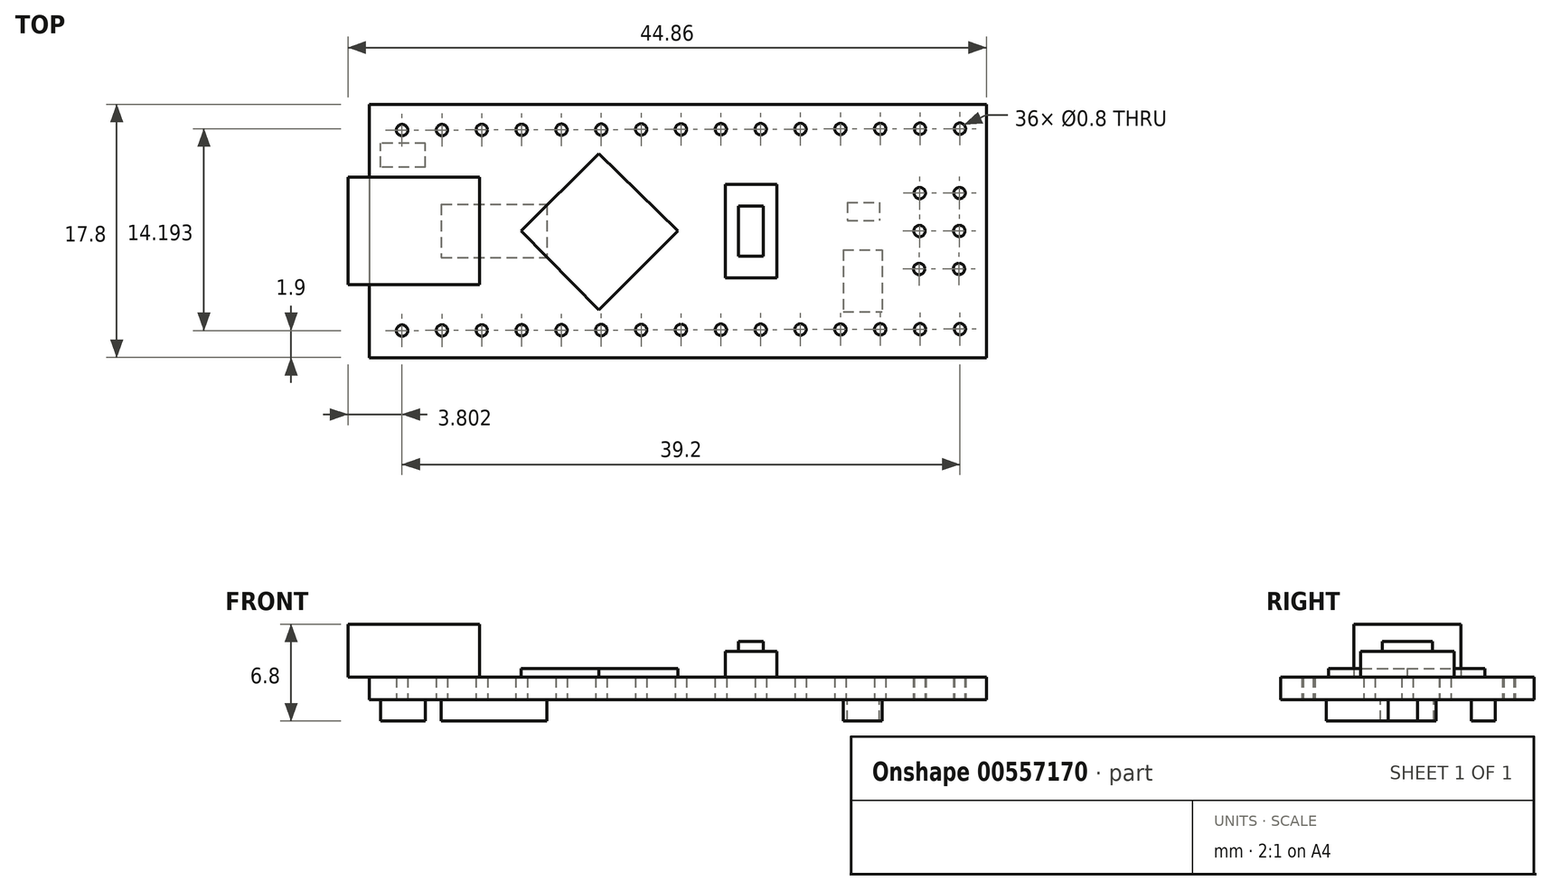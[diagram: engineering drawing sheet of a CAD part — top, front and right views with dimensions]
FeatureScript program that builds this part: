
annotation { "Feature Type Name" : "Feature", "Feature Type Description" : "" }
export const myFeature = defineFeature(function(context is Context, id is Id, definition is map)
    precondition{}
    {
        {
            var Q0;
            Q0=qCreatedBy(makeId("Top.planeOp"),FACE);
            var sketch = newSketch(context, id + "F0", { "sketchPlane" : qUnion([Q0])});
            skLineSegment(sketch, "E0.bottom", {"start": v(21.68, 8.9) * mm, "end": v(-21.67, 8.9) * mm});
            skLineSegment(sketch, "E0.top", {"start": v(21.67, -8.9) * mm, "end": v(-21.68, -8.9) * mm});
            skLineSegment(sketch, "E0.left", {"start": v(21.68, 8.9) * mm, "end": v(21.67, -8.9) * mm});
            skLineSegment(sketch, "E0.right", {"start": v(-21.67, 8.9) * mm, "end": v(-21.68, -8.9) * mm});
            skPoint(sketch, "E0.middle", {"position": v(0, 0) * mm});
            skCircle(sketch, "E1", {"center": v(-19.38, 7.1) * mm, "radius": 0.4 * mm});
            skCircle(sketch, "E2.0.3.0", {"center": v(94.43, 7.36) * mm, "radius": 0.4 * mm});
            skCircle(sketch, "E2.0.4.0", {"center": v(132.33, 7.36) * mm, "radius": 0.4 * mm});
            skCircle(sketch, "E3.1.0.0", {"center": v(-16.58, 7.1) * mm, "radius": 0.4 * mm});
            skCircle(sketch, "E3.2.0.0", {"center": v(-13.78, 7.1) * mm, "radius": 0.4 * mm});
            skCircle(sketch, "E3.3.0.0", {"center": v(-10.98, 7.11) * mm, "radius": 0.4 * mm});
            skCircle(sketch, "E3.4.0.0", {"center": v(-8.18, 7.12) * mm, "radius": 0.4 * mm});
            skCircle(sketch, "E3.5.0.0", {"center": v(-5.38, 7.13) * mm, "radius": 0.4 * mm});
            skCircle(sketch, "E3.6.0.0", {"center": v(-2.58, 7.14) * mm, "radius": 0.4 * mm});
            skCircle(sketch, "E3.7.0.0", {"center": v(0.22, 7.14) * mm, "radius": 0.4 * mm});
            skCircle(sketch, "E3.8.0.0", {"center": v(3.02, 7.15) * mm, "radius": 0.4 * mm});
            skCircle(sketch, "E3.9.0.0", {"center": v(5.82, 7.16) * mm, "radius": 0.4 * mm});
            skCircle(sketch, "E3.10.0.0", {"center": v(8.62, 7.16) * mm, "radius": 0.4 * mm});
            skCircle(sketch, "E3.11.0.0", {"center": v(11.42, 7.17) * mm, "radius": 0.4 * mm});
            skCircle(sketch, "E3.12.0.0", {"center": v(14.22, 7.18) * mm, "radius": 0.4 * mm});
            skCircle(sketch, "E3.13.0.0", {"center": v(17.02, 7.19) * mm, "radius": 0.4 * mm});
            skCircle(sketch, "E3.14.0.0", {"center": v(19.82, 7.2) * mm, "radius": 0.4 * mm});
            skLineSegment(sketch, "E4", {"start": v(-5.56, -6.44) * mm, "end": v(-0.12, -1) * mm});
            skLineSegment(sketch, "E5", {"start": v(-5.56, -6.44) * mm, "end": v(-11, -1) * mm});
            skLineSegment(sketch, "E6", {"start": v(-0.12, -1) * mm, "end": v(-5.56, 4.45) * mm});
            skLineSegment(sketch, "E7", {"start": v(-11, -1) * mm, "end": v(-5.56, 4.45) * mm});
            skLineSegment(sketch, "E8.bottom", {"start": v(3.33, -3.28) * mm, "end": v(6.96, -3.28) * mm});
            skLineSegment(sketch, "E8.top", {"start": v(3.33, 3.28) * mm, "end": v(6.96, 3.28) * mm});
            skLineSegment(sketch, "E8.left", {"start": v(3.33, -3.28) * mm, "end": v(3.33, 3.28) * mm});
            skLineSegment(sketch, "E8.right", {"start": v(6.96, -3.28) * mm, "end": v(6.96, 3.28) * mm});
            skPoint(sketch, "E8.middle", {"position": v(5.14, 0) * mm});
            skLineSegment(sketch, "E9.bottom", {"start": v(4.27, -1.76) * mm, "end": v(6.01, -1.76) * mm});
            skLineSegment(sketch, "E9.top", {"start": v(4.27, 1.76) * mm, "end": v(6.01, 1.76) * mm});
            skLineSegment(sketch, "E9.left", {"start": v(4.27, -1.76) * mm, "end": v(4.27, 1.76) * mm});
            skLineSegment(sketch, "E9.right", {"start": v(6.01, -1.76) * mm, "end": v(6.01, 1.76) * mm});
            skCircle(sketch, "E10.1.0.0", {"center": v(19.8, 2.67) * mm, "radius": 0.4 * mm});
            skCircle(sketch, "E10.1.0.1", {"center": v(17, 2.66) * mm, "radius": 0.4 * mm});
            skCircle(sketch, "E10.2.0.0", {"center": v(19.78, 0) * mm, "radius": 0.4 * mm});
            skCircle(sketch, "E10.2.0.1", {"center": v(16.98, 0) * mm, "radius": 0.4 * mm});
            skCircle(sketch, "E10.3.0.0", {"center": v(19.76, -2.66) * mm, "radius": 0.4 * mm});
            skCircle(sketch, "E10.3.0.1", {"center": v(16.96, -2.67) * mm, "radius": 0.4 * mm});
            skCircle(sketch, "E11", {"center": v(-19.38, -7) * mm, "radius": 0.4 * mm});
            skCircle(sketch, "E12.1.0.0", {"center": v(-16.58, -7) * mm, "radius": 0.4 * mm});
            skCircle(sketch, "E12.2.0.0", {"center": v(-13.78, -6.99) * mm, "radius": 0.4 * mm});
            skCircle(sketch, "E12.3.0.0", {"center": v(-10.98, -6.98) * mm, "radius": 0.4 * mm});
            skCircle(sketch, "E12.4.0.0", {"center": v(-8.18, -6.97) * mm, "radius": 0.4 * mm});
            skCircle(sketch, "E12.5.0.0", {"center": v(-5.38, -6.96) * mm, "radius": 0.4 * mm});
            skCircle(sketch, "E12.6.0.0", {"center": v(-2.58, -6.96) * mm, "radius": 0.4 * mm});
            skCircle(sketch, "E12.7.0.0", {"center": v(0.22, -6.95) * mm, "radius": 0.4 * mm});
            skCircle(sketch, "E12.8.0.0", {"center": v(3.02, -6.94) * mm, "radius": 0.4 * mm});
            skCircle(sketch, "E12.9.0.0", {"center": v(5.82, -6.94) * mm, "radius": 0.4 * mm});
            skCircle(sketch, "E12.10.0.0", {"center": v(8.62, -6.93) * mm, "radius": 0.4 * mm});
            skCircle(sketch, "E12.11.0.0", {"center": v(11.42, -6.92) * mm, "radius": 0.4 * mm});
            skCircle(sketch, "E12.12.0.0", {"center": v(14.22, -6.91) * mm, "radius": 0.4 * mm});
            skCircle(sketch, "E12.13.0.0", {"center": v(17.02, -6.9) * mm, "radius": 0.4 * mm});
            skCircle(sketch, "E12.14.0.0", {"center": v(19.82, -6.9) * mm, "radius": 0.4 * mm});
            skLineSegment(sketch, "E13.bottom", {"start": v(-23.18, 3.77) * mm, "end": v(-13.94, 3.77) * mm});
            skLineSegment(sketch, "E13.top", {"start": v(-23.18, -3.77) * mm, "end": v(-13.94, -3.77) * mm});
            skLineSegment(sketch, "E13.left", {"start": v(-23.18, 3.77) * mm, "end": v(-23.18, -3.77) * mm});
            skLineSegment(sketch, "E13.right", {"start": v(-13.94, 3.77) * mm, "end": v(-13.94, -3.77) * mm});
            skPoint(sketch, "E13.middle", {"position": v(-18.56, 0) * mm});
            skPoint(sketch, "E13.middle.positionSnap0", {"position": v(-21.68, 0) * mm});
            skPoint(sketch, "E13.centerSnap0", {"position": v(-21.68, 0) * mm});
            skLineSegment(sketch, "E14", {"start": v(-21.68, 0) * mm, "end": v(21.68, 0) * mm, "construction": true});
            skSolve(sketch);
        }
        {
            var Q0;
            Q0=makeQuery(id+"F0.imprint","IMPRINT",FACE,{"disambiguationData":[TD([[makeQuery(id+"F0.imprint","IMPRINT",EDGE,{"derivedFrom":sQuery(id+"F0.wireOp",EDGE,"E0.bottom")}),1.0]])]});
            var Q1;
            {var subQ5=sQuery(id+"F0.wireOp",EDGE,"E13.right");Q1=makeQuery(id+"F0.imprint","IMPRINT",FACE,{"disambiguationData":[TD([[makeQuery(id+"F0.imprint","IMPRINT",EDGE,{"derivedFrom":subQ5}),-1.0]])]});}
            var Q2;
            Q2=makeQuery(id+"F0.imprint","IMPRINT",FACE,{"disambiguationData":[TD([[makeQuery(id+"F0.imprint","IMPRINT",EDGE,{"derivedFrom":sQuery(id+"F0.wireOp",EDGE,"E4")}),1.0]])]});
            var Q3;
            Q3=makeQuery(id+"F0.imprint","IMPRINT",FACE,{"disambiguationData":[TD([[makeQuery(id+"F0.imprint","IMPRINT",EDGE,{"derivedFrom":sQuery(id+"F0.wireOp",EDGE,"E8.bottom")}),1.0]])]});
            var Q4;
            Q4=makeQuery(id+"F0.imprint","IMPRINT",FACE,{"disambiguationData":[TD([[makeQuery(id+"F0.imprint","IMPRINT",EDGE,{"derivedFrom":sQuery(id+"F0.wireOp",EDGE,"E9.bottom")}),1.0]])]});
            extrude(context, id + "F1", {"entities" : qUnion([Q0, Q1, Q2, Q3, Q4]), "endBound" : BoundingType.SYMMETRIC, "depth" : 1.6 * mm, "offsetDistance" : 25 * mm});
        }
        {
            var Q0;
            Q0=makeQuery(id+"F1.opExtrude","CAP_FACE",FACE,{"disambiguationData":[OSD([sQuery(id+"F0.wireOp",EDGE,"E0.bottom"),sQuery(id+"F0.wireOp",EDGE,"E0.top"),sQuery(id+"F0.wireOp",EDGE,"E0.left"),sQuery(id+"F0.wireOp",EDGE,"E0.right"),sQuery(id+"F0.wireOp",EDGE,"E1"),sQuery(id+"F0.wireOp",EDGE,"E3.1.0.0"),sQuery(id+"F0.wireOp",EDGE,"E3.2.0.0"),sQuery(id+"F0.wireOp",EDGE,"E3.3.0.0"),sQuery(id+"F0.wireOp",EDGE,"E3.4.0.0"),sQuery(id+"F0.wireOp",EDGE,"E3.5.0.0"),sQuery(id+"F0.wireOp",EDGE,"E3.6.0.0"),sQuery(id+"F0.wireOp",EDGE,"E3.7.0.0"),sQuery(id+"F0.wireOp",EDGE,"E3.8.0.0"),sQuery(id+"F0.wireOp",EDGE,"E3.9.0.0"),sQuery(id+"F0.wireOp",EDGE,"E3.10.0.0"),sQuery(id+"F0.wireOp",EDGE,"E3.11.0.0"),sQuery(id+"F0.wireOp",EDGE,"E3.12.0.0"),sQuery(id+"F0.wireOp",EDGE,"E3.13.0.0"),sQuery(id+"F0.wireOp",EDGE,"E3.14.0.0"),sQuery(id+"F0.wireOp",EDGE,"E10.1.0.0"),sQuery(id+"F0.wireOp",EDGE,"E10.1.0.1"),sQuery(id+"F0.wireOp",EDGE,"E10.2.0.0"),sQuery(id+"F0.wireOp",EDGE,"E10.2.0.1"),sQuery(id+"F0.wireOp",EDGE,"E10.3.0.0"),sQuery(id+"F0.wireOp",EDGE,"E10.3.0.1"),sQuery(id+"F0.wireOp",EDGE,"E11"),sQuery(id+"F0.wireOp",EDGE,"E12.1.0.0"),sQuery(id+"F0.wireOp",EDGE,"E12.2.0.0"),sQuery(id+"F0.wireOp",EDGE,"E12.3.0.0"),sQuery(id+"F0.wireOp",EDGE,"E12.4.0.0"),sQuery(id+"F0.wireOp",EDGE,"E12.5.0.0"),sQuery(id+"F0.wireOp",EDGE,"E12.6.0.0"),sQuery(id+"F0.wireOp",EDGE,"E12.7.0.0"),sQuery(id+"F0.wireOp",EDGE,"E12.8.0.0"),sQuery(id+"F0.wireOp",EDGE,"E12.9.0.0"),sQuery(id+"F0.wireOp",EDGE,"E12.10.0.0"),sQuery(id+"F0.wireOp",EDGE,"E12.11.0.0"),sQuery(id+"F0.wireOp",EDGE,"E12.12.0.0"),sQuery(id+"F0.wireOp",EDGE,"E12.13.0.0"),sQuery(id+"F0.wireOp",EDGE,"E12.14.0.0")])],"isStart":false});
            var sketch = newSketch(context, id + "F2", { "sketchPlane" : qUnion([Q0])});
            skLineSegment(sketch, "E15.0", {"start": v(-23.18, 3.77) * mm, "end": v(-13.94, 3.77) * mm});
            skLineSegment(sketch, "E15.1", {"start": v(-13.94, 3.77) * mm, "end": v(-13.94, -3.77) * mm});
            skLineSegment(sketch, "E15.2", {"start": v(-23.18, -3.77) * mm, "end": v(-13.94, -3.77) * mm});
            skLineSegment(sketch, "E15.3", {"start": v(-23.18, 3.77) * mm, "end": v(-23.18, -3.77) * mm});
            skLineSegment(sketch, "E15.4", {"start": v(-11, 0) * mm, "end": v(-5.56, 5.44) * mm});
            skLineSegment(sketch, "E15.5", {"start": v(0, 0) * mm, "end": v(-5.56, 5.44) * mm});
            skLineSegment(sketch, "E15.6", {"start": v(-5.56, -5.54) * mm, "end": v(0, 0) * mm});
            skLineSegment(sketch, "E15.7", {"start": v(-5.56, -5.54) * mm, "end": v(-11, 0) * mm});
            skLineSegment(sketch, "E15.8", {"start": v(6.96, -3.28) * mm, "end": v(6.96, 3.28) * mm});
            skLineSegment(sketch, "E15.9", {"start": v(3.33, 3.28) * mm, "end": v(6.96, 3.28) * mm});
            skLineSegment(sketch, "E15.10", {"start": v(3.33, -3.28) * mm, "end": v(6.96, -3.28) * mm});
            skLineSegment(sketch, "E15.11", {"start": v(3.33, -3.28) * mm, "end": v(3.33, 3.28) * mm});
            skLineSegment(sketch, "E15.12", {"start": v(4.27, 1.76) * mm, "end": v(6.01, 1.76) * mm});
            skLineSegment(sketch, "E15.13", {"start": v(6.01, -1.76) * mm, "end": v(6.01, 1.76) * mm});
            skLineSegment(sketch, "E15.14", {"start": v(4.27, -1.76) * mm, "end": v(4.27, 1.76) * mm});
            skLineSegment(sketch, "E15.15", {"start": v(4.27, -1.76) * mm, "end": v(6.01, -1.76) * mm});
            skLineSegment(sketch, "E16.0", {"start": v(-21.68, 0) * mm, "end": v(21.68, 0) * mm, "construction": true});
            skSolve(sketch);
        }
        {
            var Q0;
            {var subQ0=sQuery(id+"F2.wireOp",EDGE,"E15.3");Q0=makeQuery(id+"F2.imprint","IMPRINT",FACE,{"disambiguationData":[TD([[makeQuery(id+"F2.imprint","IMPRINT",EDGE,{"derivedFrom":subQ0}),1.0]])]});}
            var Q1;
            {var subQ0=sQuery(id+"F2.wireOp",EDGE,"E15.1");Q1=makeQuery(id+"F2.imprint","IMPRINT",FACE,{"disambiguationData":[TD([[makeQuery(id+"F2.imprint","IMPRINT",EDGE,{"derivedFrom":subQ0}),-1.0]])]});}
            extrude(context, id + "F3", {"entities" : qUnion([Q0, Q1]), "operationType" : NewBodyOperationType.ADD, "depth" : 3.7 * mm, "offsetDistance" : 25 * mm});
        }
        {
            var Q0;
            Q0=makeQuery(id+"F2.imprint","IMPRINT",FACE,{"disambiguationData":[TD([[makeQuery(id+"F2.imprint","IMPRINT",EDGE,{"derivedFrom":sQuery(id+"F2.wireOp",EDGE,"E15.4")}),-1.0]])]});
            var Q1;
            Q1=sQuery(id+"F0.wireOp",EDGE,"E7");
            var Q2;
            Q2=sQuery(id+"F0.wireOp",EDGE,"E6");
            var Q3;
            Q3=sQuery(id+"F0.wireOp",EDGE,"E4");
            var Q4;
            Q4=sQuery(id+"F0.wireOp",EDGE,"E5");
            extrude(context, id + "F4", {"entities" : qUnion([Q0]), "operationType" : NewBodyOperationType.ADD, "surfaceEntities" : qUnion([Q1, Q2, Q3, Q4]), "depth" : .6 * mm, "offsetDistance" : 25 * mm});
        }
        {
            var Q0;
            Q0=makeQuery(id+"F2.imprint","IMPRINT",FACE,{"disambiguationData":[TD([[makeQuery(id+"F2.imprint","IMPRINT",EDGE,{"derivedFrom":sQuery(id+"F2.wireOp",EDGE,"E15.8")}),1.0]])]});
            extrude(context, id + "F5", {"entities" : qUnion([Q0]), "operationType" : NewBodyOperationType.ADD, "depth" : 1.8 * mm, "offsetDistance" : 25 * mm});
        }
        {
            var Q0;
            Q0=makeQuery(id+"F2.imprint","IMPRINT",FACE,{"disambiguationData":[TD([[makeQuery(id+"F2.imprint","IMPRINT",EDGE,{"derivedFrom":sQuery(id+"F2.wireOp",EDGE,"E15.12")}),-1.0]])]});
            extrude(context, id + "F6", {"entities" : qUnion([Q0]), "operationType" : NewBodyOperationType.ADD, "depth" : 2.5 * mm, "offsetDistance" : 25 * mm});
        }
        {
            var Q0;
            Q0=makeQuery(id+"F1.opExtrude","CAP_FACE",FACE,{"disambiguationData":[OSD([sQuery(id+"F0.wireOp",EDGE,"E0.bottom"),sQuery(id+"F0.wireOp",EDGE,"E0.top"),sQuery(id+"F0.wireOp",EDGE,"E0.left"),sQuery(id+"F0.wireOp",EDGE,"E0.right"),sQuery(id+"F0.wireOp",EDGE,"E1"),sQuery(id+"F0.wireOp",EDGE,"E3.1.0.0"),sQuery(id+"F0.wireOp",EDGE,"E3.2.0.0"),sQuery(id+"F0.wireOp",EDGE,"E3.3.0.0"),sQuery(id+"F0.wireOp",EDGE,"E3.4.0.0"),sQuery(id+"F0.wireOp",EDGE,"E3.5.0.0"),sQuery(id+"F0.wireOp",EDGE,"E3.6.0.0"),sQuery(id+"F0.wireOp",EDGE,"E3.7.0.0"),sQuery(id+"F0.wireOp",EDGE,"E3.8.0.0"),sQuery(id+"F0.wireOp",EDGE,"E3.9.0.0"),sQuery(id+"F0.wireOp",EDGE,"E3.10.0.0"),sQuery(id+"F0.wireOp",EDGE,"E3.11.0.0"),sQuery(id+"F0.wireOp",EDGE,"E3.12.0.0"),sQuery(id+"F0.wireOp",EDGE,"E3.13.0.0"),sQuery(id+"F0.wireOp",EDGE,"E3.14.0.0"),sQuery(id+"F0.wireOp",EDGE,"E10.1.0.0"),sQuery(id+"F0.wireOp",EDGE,"E10.1.0.1"),sQuery(id+"F0.wireOp",EDGE,"E10.2.0.0"),sQuery(id+"F0.wireOp",EDGE,"E10.2.0.1"),sQuery(id+"F0.wireOp",EDGE,"E10.3.0.0"),sQuery(id+"F0.wireOp",EDGE,"E10.3.0.1"),sQuery(id+"F0.wireOp",EDGE,"E11"),sQuery(id+"F0.wireOp",EDGE,"E12.1.0.0"),sQuery(id+"F0.wireOp",EDGE,"E12.2.0.0"),sQuery(id+"F0.wireOp",EDGE,"E12.3.0.0"),sQuery(id+"F0.wireOp",EDGE,"E12.4.0.0"),sQuery(id+"F0.wireOp",EDGE,"E12.5.0.0"),sQuery(id+"F0.wireOp",EDGE,"E12.6.0.0"),sQuery(id+"F0.wireOp",EDGE,"E12.7.0.0"),sQuery(id+"F0.wireOp",EDGE,"E12.8.0.0"),sQuery(id+"F0.wireOp",EDGE,"E12.9.0.0"),sQuery(id+"F0.wireOp",EDGE,"E12.10.0.0"),sQuery(id+"F0.wireOp",EDGE,"E12.11.0.0"),sQuery(id+"F0.wireOp",EDGE,"E12.12.0.0"),sQuery(id+"F0.wireOp",EDGE,"E12.13.0.0"),sQuery(id+"F0.wireOp",EDGE,"E12.14.0.0")])],"isStart":true});
            var sketch = newSketch(context, id + "F7", { "sketchPlane" : qUnion([Q0])});
            skLineSegment(sketch, "E17.0", {"start": v(-21.68, 0) * mm, "end": v(21.68, 0) * mm, "construction": true});
            skLineSegment(sketch, "E18.bottom", {"start": v(-16.63, -1.87) * mm, "end": v(-9.2, -1.87) * mm});
            skLineSegment(sketch, "E18.top", {"start": v(-16.63, 1.87) * mm, "end": v(-9.2, 1.87) * mm});
            skLineSegment(sketch, "E18.left", {"start": v(-16.63, -1.87) * mm, "end": v(-16.63, 1.87) * mm});
            skLineSegment(sketch, "E18.right", {"start": v(-9.2, -1.87) * mm, "end": v(-9.2, 1.87) * mm});
            skPoint(sketch, "E18.middle", {"position": v(-12.92, 0) * mm});
            skLineSegment(sketch, "E19.bottom", {"start": v(11.61, 1.33) * mm, "end": v(14.37, 1.33) * mm});
            skLineSegment(sketch, "E19.top", {"start": v(11.61, 5.68) * mm, "end": v(14.37, 5.68) * mm});
            skLineSegment(sketch, "E19.left", {"start": v(11.61, 1.33) * mm, "end": v(11.61, 5.68) * mm});
            skLineSegment(sketch, "E19.right", {"start": v(14.37, 1.33) * mm, "end": v(14.37, 5.68) * mm});
            skPoint(sketch, "E19.middle", {"position": v(13, 3.5) * mm});
            skLineSegment(sketch, "E20.bottom", {"start": v(11.9, -2.01) * mm, "end": v(14.15, -2.01) * mm});
            skLineSegment(sketch, "E20.top", {"start": v(11.9, -0.72) * mm, "end": v(14.15, -0.72) * mm});
            skLineSegment(sketch, "E20.left", {"start": v(11.9, -2.01) * mm, "end": v(11.9, -0.72) * mm});
            skLineSegment(sketch, "E20.right", {"start": v(14.15, -2.01) * mm, "end": v(14.15, -0.72) * mm});
            skPoint(sketch, "E20.middle", {"position": v(13.02, -1.37) * mm});
            skLineSegment(sketch, "E21.bottom", {"start": v(-17.73, -4.49) * mm, "end": v(-20.87, -4.49) * mm});
            skLineSegment(sketch, "E21.top", {"start": v(-17.73, -6.17) * mm, "end": v(-20.87, -6.17) * mm});
            skLineSegment(sketch, "E21.left", {"start": v(-17.73, -4.49) * mm, "end": v(-17.73, -6.17) * mm});
            skLineSegment(sketch, "E21.right", {"start": v(-20.87, -4.49) * mm, "end": v(-20.87, -6.17) * mm});
            skPoint(sketch, "E21.middle", {"position": v(-19.3, -5.33) * mm});
            skSolve(sketch);
        }
        {
            var Q0;
            Q0=makeQuery(id+"F7.imprint","IMPRINT",FACE,{"disambiguationData":[TD([[makeQuery(id+"F7.imprint","IMPRINT",EDGE,{"derivedFrom":sQuery(id+"F7.wireOp",EDGE,"E21.bottom")}),1.0]])]});
            var Q1;
            Q1=makeQuery(id+"F7.imprint","IMPRINT",FACE,{"disambiguationData":[TD([[makeQuery(id+"F7.imprint","IMPRINT",EDGE,{"derivedFrom":sQuery(id+"F7.wireOp",EDGE,"E18.bottom")}),1.0]])]});
            var Q2;
            Q2=makeQuery(id+"F7.imprint","IMPRINT",FACE,{"disambiguationData":[TD([[makeQuery(id+"F7.imprint","IMPRINT",EDGE,{"derivedFrom":sQuery(id+"F7.wireOp",EDGE,"E19.bottom")}),1.0]])]});
            var Q3;
            Q3=makeQuery(id+"F7.imprint","IMPRINT",FACE,{"disambiguationData":[TD([[makeQuery(id+"F7.imprint","IMPRINT",EDGE,{"derivedFrom":sQuery(id+"F7.wireOp",EDGE,"E20.bottom")}),1.0]])]});
            extrude(context, id + "F8", {"entities" : qUnion([Q0, Q1, Q2, Q3]), "operationType" : NewBodyOperationType.ADD, "depth" : 1.5 * mm, "offsetDistance" : 25 * mm});
        }
    });
